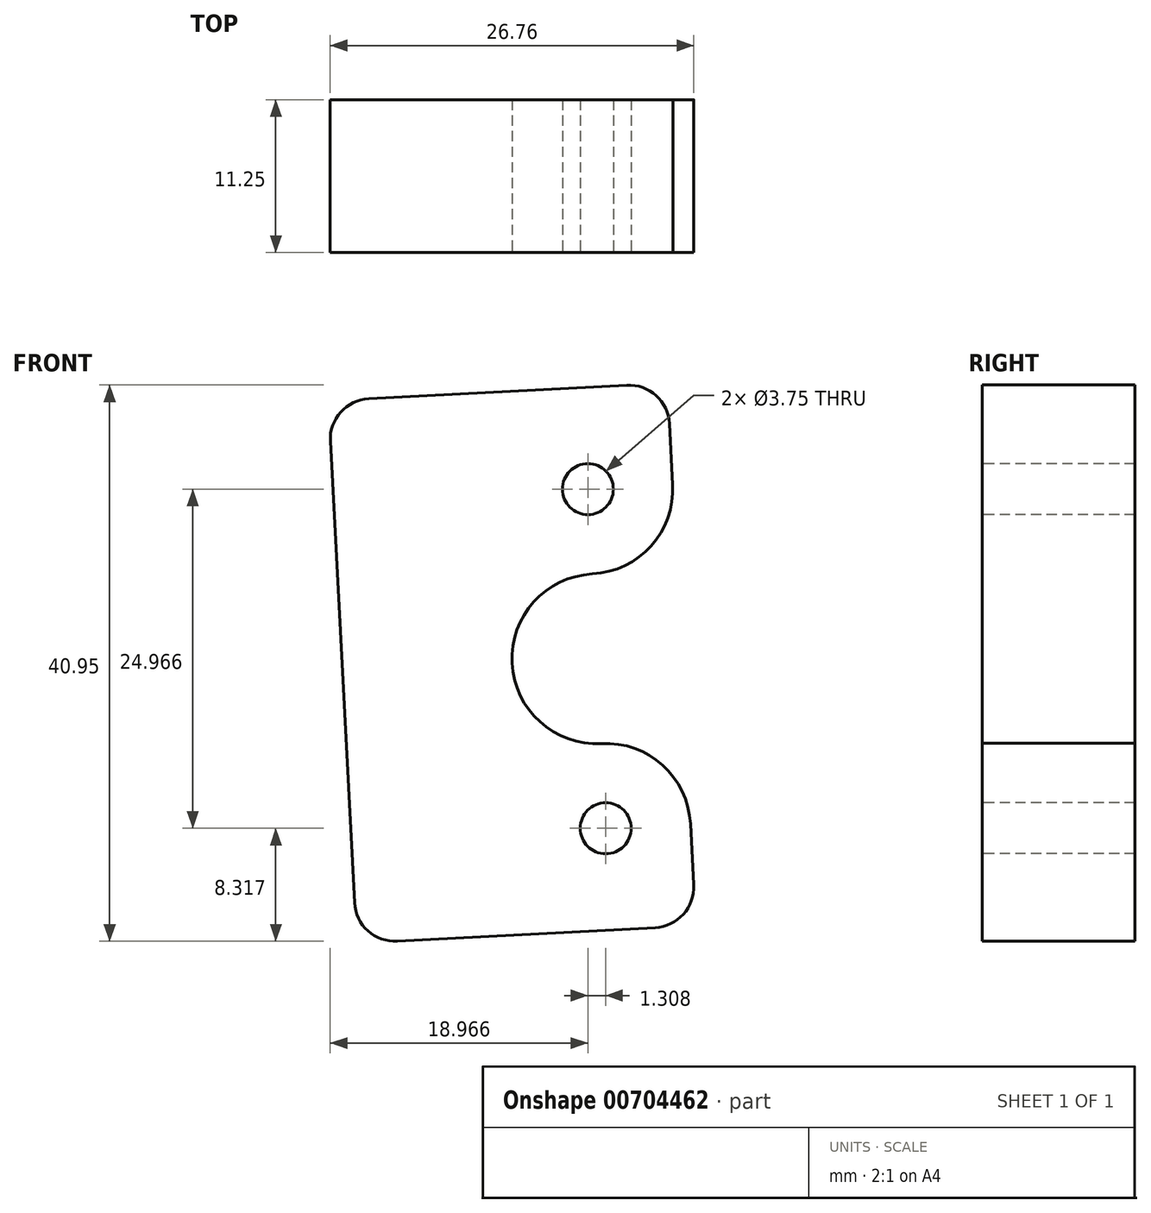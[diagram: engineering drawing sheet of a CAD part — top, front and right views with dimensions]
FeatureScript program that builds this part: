
annotation { "Feature Type Name" : "Feature", "Feature Type Description" : "" }
export const myFeature = defineFeature(function(context is Context, id is Id, definition is map)
    precondition{}
    {
        {
            var Q0;
            Q0=qCreatedBy(makeId("Front.planeOp"),FACE);
            var sketch = newSketch(context, id + "F0", { "sketchPlane" : qUnion([Q0])});
            skCircle(sketch, "E0", {"center": v(0, 0) * mm, "radius": 17.9 * mm, "construction": true});
            skArc(sketch, "E1", {"start": v(0, 6.25) * mm, "mid": v(-6.25, -0.16) * mm, "end": v(0.33, -6.24) * mm, "construction": true});
            skLineSegment(sketch, "E2", {"start": v(0, 17.9) * mm, "end": v(0, -17.9) * mm, "construction": true});
            skLineSegment(sketch, "E3", {"start": v(0, 0) * mm, "end": v(-0.94, 17.88) * mm, "construction": true});
            skLineSegment(sketch, "E4", {"start": v(0, 0) * mm, "end": v(0.94, -17.88) * mm, "construction": true});
            skCircle(sketch, "E5", {"center": v(-0.65, 12.48) * mm, "radius": 1.88 * mm});
            skLineSegment(sketch, "E6", {"start": v(0, 0) * mm, "end": v(17.88, 0.94) * mm, "construction": true});
            skCircle(sketch, "E7.MirrorC", {"center": v(0.65, -12.48) * mm, "radius": 1.88 * mm});
            skLineSegment(sketch, "E8", {"start": v(5.59, 12.8) * mm, "end": v(5.35, 17.3) * mm});
            skLineSegment(sketch, "E9", {"start": v(2.2, 20.14) * mm, "end": v(-16.78, 19.15) * mm});
            skLineSegment(sketch, "E10", {"start": v(-19.61, 16) * mm, "end": v(-18.72, -0.98) * mm});
            skLineSegment(sketch, "E11.MirrorCS", {"start": v(6.9, -12.16) * mm, "end": v(7.13, -16.65) * mm});
            skLineSegment(sketch, "E12.MirrorCS", {"start": v(4.3, -19.8) * mm, "end": v(-14.68, -20.8) * mm});
            skLineSegment(sketch, "E13.MirrorCS", {"start": v(-17.83, -17.96) * mm, "end": v(-18.72, -0.98) * mm});
            skArc(sketch, "E14", {"start": v(-0.33, 6.24) * mm, "mid": v(4, 8.3) * mm, "end": v(5.59, 12.8) * mm});
            skArc(sketch, "E15.MirrorC", {"start": v(-2.82, -17.68) * mm, "mid": v(-2.43, -7.05) * mm, "end": v(6.9, -12.16) * mm});
            skArc(sketch, "E16", {"start": v(0, 6.25) * mm, "mid": v(-6.25, -0.16) * mm, "end": v(0.33, -6.24) * mm});
            skPoint(sketch, "E17.visualSharp", {"position": v(5.2, 20.3) * mm});
            skArc(sketch, "E17.filletArc", {"start": v(5.35, 17.3) * mm, "mid": v(4.36, 19.38) * mm, "end": v(2.2, 20.14) * mm});
            skPoint(sketch, "E18.visualSharp", {"position": v(-19.77, 19) * mm});
            skArc(sketch, "E18.filletArc", {"start": v(-16.78, 19.15) * mm, "mid": v(-18.85, 18.16) * mm, "end": v(-19.61, 16) * mm});
            skPoint(sketch, "E19.visualSharp", {"position": v(-17.68, -20.95) * mm});
            skArc(sketch, "E19.filletArc", {"start": v(-17.83, -17.96) * mm, "mid": v(-16.85, -20.03) * mm, "end": v(-14.68, -20.8) * mm});
            skPoint(sketch, "E20.visualSharp", {"position": v(7.29, -19.65) * mm});
            skArc(sketch, "E20.filletArc", {"start": v(4.3, -19.8) * mm, "mid": v(6.36, -18.81) * mm, "end": v(7.13, -16.65) * mm});
            skSolve(sketch);
        }
        {
            var Q0;
            Q0=makeQuery(id+"F0.imprint","IMPRINT",FACE,{"disambiguationData":[TD([[makeQuery(id+"F0.imprint","IMPRINT",EDGE,{"derivedFrom":sQuery(id+"F0.wireOp",EDGE,"E5")}),-1.0]])]});
            extrude(context, id + "F1", {"entities" : qUnion([Q0]), "oppositeDirection" : true, "depth" : 11.25 * mm, "offsetDistance" : 25 * mm});
        }
    });
